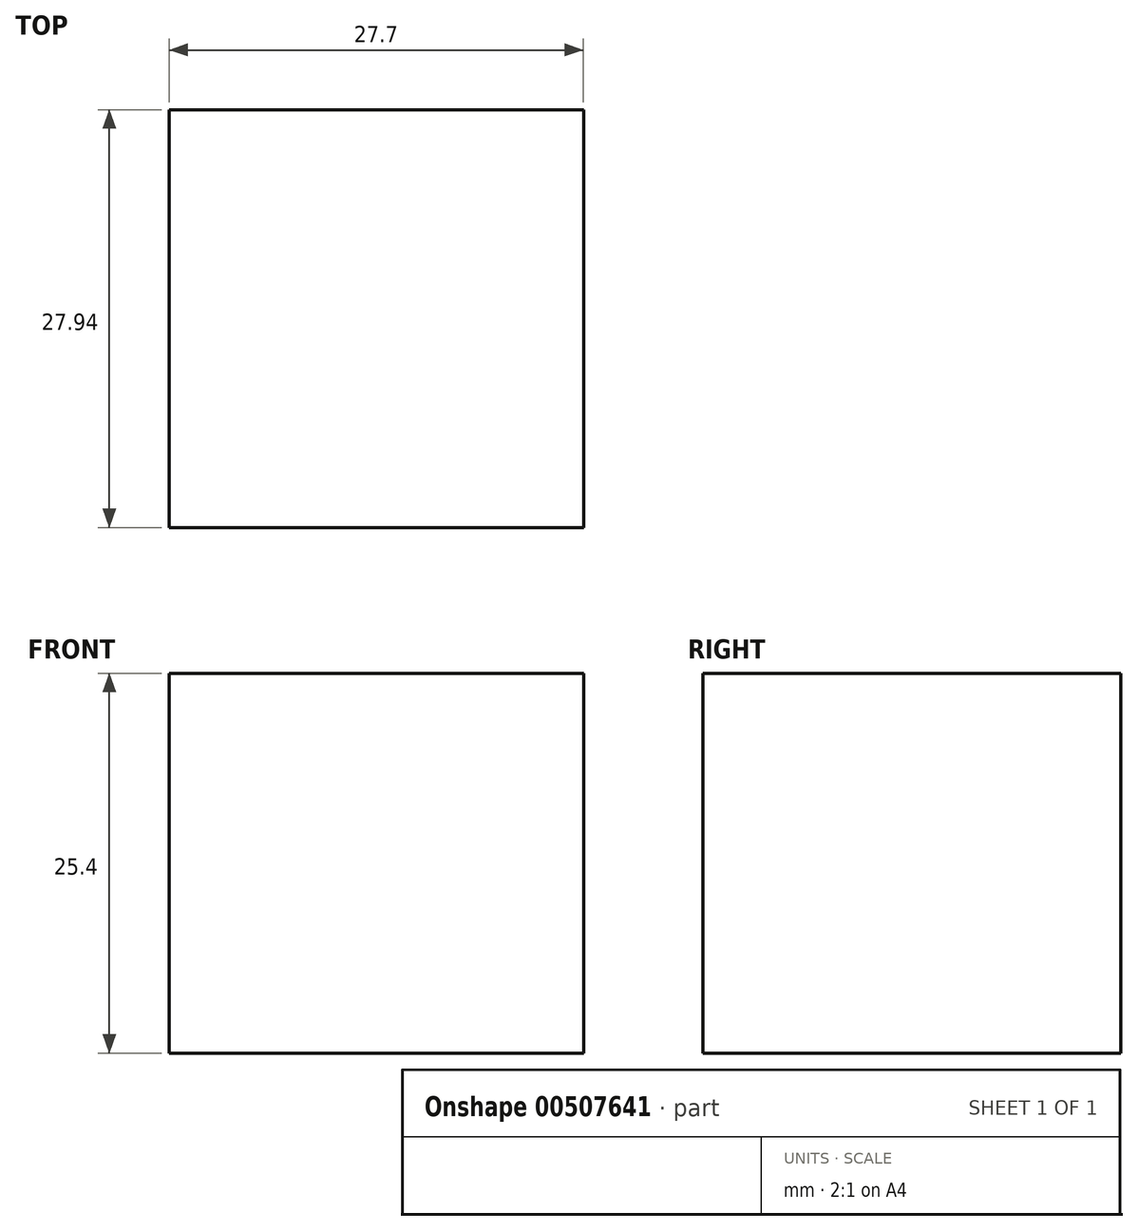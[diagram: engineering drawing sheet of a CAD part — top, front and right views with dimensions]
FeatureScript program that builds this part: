
annotation { "Feature Type Name" : "Feature", "Feature Type Description" : "" }
export const myFeature = defineFeature(function(context is Context, id is Id, definition is map)
    precondition{}
    {
        {
            var Q0;
            Q0=qCreatedBy(makeId("Top.planeOp"),FACE);
            var sketch = newSketch(context, id + "F0", { "sketchPlane" : qUnion([Q0])});
            skLineSegment(sketch, "E0.bottom", {"start": v(-13.85, 13.97) * mm, "end": v(13.85, 13.97) * mm});
            skLineSegment(sketch, "E0.top", {"start": v(-13.85, -13.97) * mm, "end": v(13.85, -13.97) * mm});
            skLineSegment(sketch, "E0.left", {"start": v(-13.85, 13.97) * mm, "end": v(-13.85, -13.97) * mm});
            skLineSegment(sketch, "E0.right", {"start": v(13.85, 13.97) * mm, "end": v(13.85, -13.97) * mm});
            skPoint(sketch, "E0.middle", {"position": v(0, 0) * mm});
            skSolve(sketch);
        }
        {
            var Q0;
            Q0 = qSketchRegion(id + "F0", true);
            extrude(context, id + "F1", {"entities" : qUnion([Q0]), "depth" : 25.4 * mm});
        }
    });
